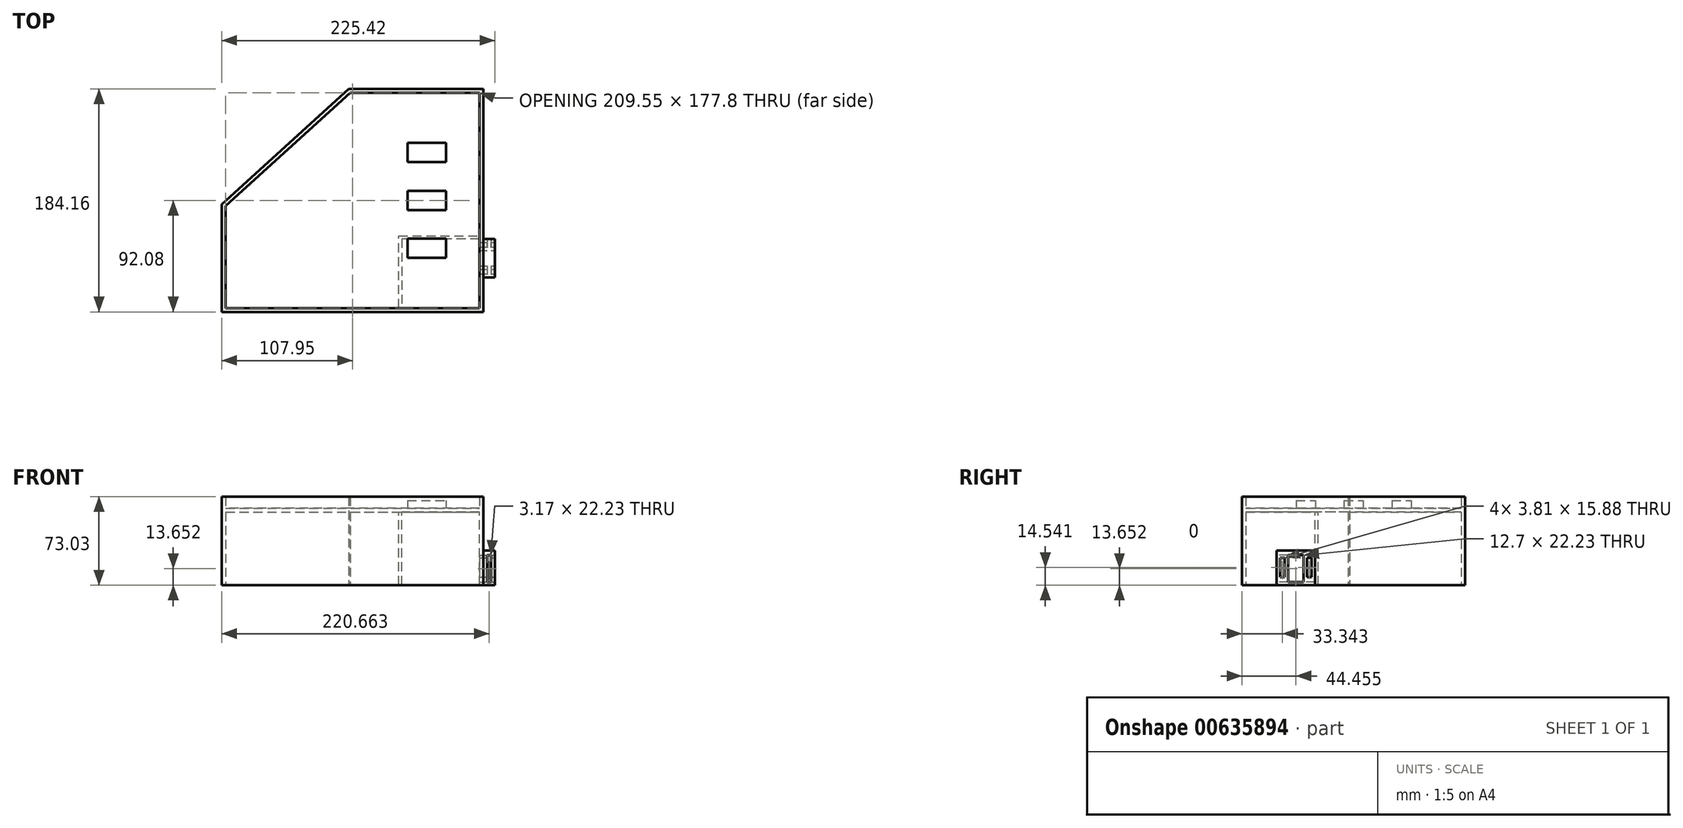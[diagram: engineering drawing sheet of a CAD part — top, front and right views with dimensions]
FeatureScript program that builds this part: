
annotation { "Feature Type Name" : "Feature", "Feature Type Description" : "" }
export const myFeature = defineFeature(function(context is Context, id is Id, definition is map)
    precondition{}
    {
        {
            var Q0;
            Q0=qCreatedBy(makeId("Top.planeOp"),FACE);
            var sketch = newSketch(context, id + "F0", { "sketchPlane" : qUnion([Q0])});
            skLineSegment(sketch, "E0.bottom", {"start": v(-3.18, 92.08) * mm, "end": v(107.95, 92.08) * mm});
            skLineSegment(sketch, "E0.top", {"start": v(-107.95, -92.08) * mm, "end": v(107.95, -92.08) * mm});
            skLineSegment(sketch, "E0.left", {"start": v(-107.95, -3.18) * mm, "end": v(-107.95, -92.07) * mm});
            skLineSegment(sketch, "E0.right", {"start": v(107.95, 92.07) * mm, "end": v(107.95, -92.08) * mm});
            skPoint(sketch, "E0.middle", {"position": v(0, 0) * mm});
            skLineSegment(sketch, "E1", {"start": v(-107.95, -3.18) * mm, "end": v(-3.18, 92.08) * mm});
            skPoint(sketch, "E2.orphan", {"position": v(-107.95, 92.08) * mm});
            skSolve(sketch);
        }
        {
            var Q0;
            Q0 = qSketchRegion(id + "F0", true);
            extrude(context, id + "F1", {"entities" : qUnion([Q0]), "depth" : 63.5 * mm, "offsetDistance" : 25.4 * mm});
        }
        {
            var Q0;
            Q0=makeQuery(id+"F1.opExtrude","CAP_FACE",FACE,{"disambiguationData":[OSD([sQuery(id+"F0.wireOp",EDGE,"E0.bottom"),sQuery(id+"F0.wireOp",EDGE,"E0.top"),sQuery(id+"F0.wireOp",EDGE,"E0.left"),sQuery(id+"F0.wireOp",EDGE,"E0.right"),sQuery(id+"F0.wireOp",EDGE,"E1")])],"isStart":true});
            shell(context, id + "F2", {"entities" : qUnion([Q0]), "thickness" : 3.17 * mm});
        }
        {
            var Q0;
            Q0=makeQuery(id+"F1.opExtrude","CAP_FACE",FACE,{"disambiguationData":[OSD([sQuery(id+"F0.wireOp",EDGE,"E0.bottom"),sQuery(id+"F0.wireOp",EDGE,"E0.top"),sQuery(id+"F0.wireOp",EDGE,"E0.left"),sQuery(id+"F0.wireOp",EDGE,"E0.right"),sQuery(id+"F0.wireOp",EDGE,"E1")])],"isStart":false});
            var sketch = newSketch(context, id + "F3", { "sketchPlane" : qUnion([Q0])});
            skLineSegment(sketch, "E3.0.0", {"start": v(-3.18, 92.08) * mm, "end": v(-107.95, -3.18) * mm});
            skLineSegment(sketch, "E3.0.1", {"start": v(-107.95, -3.18) * mm, "end": v(-107.95, -92.07) * mm});
            skLineSegment(sketch, "E3.0.2", {"start": v(-107.95, -92.08) * mm, "end": v(107.95, -92.08) * mm});
            skLineSegment(sketch, "E3.0.3", {"start": v(107.95, -92.08) * mm, "end": v(107.95, 92.07) * mm});
            skLineSegment(sketch, "E3.0.4", {"start": v(107.95, 92.08) * mm, "end": v(-3.18, 92.08) * mm});
            skLineSegment(sketch, "E4.0", {"start": v(-104.78, -88.9) * mm, "end": v(104.77, -88.9) * mm});
            skLineSegment(sketch, "E4.1", {"start": v(-104.78, -4.58) * mm, "end": v(-104.78, -88.9) * mm});
            skLineSegment(sketch, "E4.2", {"start": v(104.77, -88.9) * mm, "end": v(104.78, 88.9) * mm});
            skLineSegment(sketch, "E4.3", {"start": v(104.78, 88.9) * mm, "end": v(-1.95, 88.9) * mm});
            skLineSegment(sketch, "E4.4", {"start": v(-1.95, 88.9) * mm, "end": v(-104.78, -4.58) * mm});
            skSolve(sketch);
        }
        {
            var Q0;
            Q0 = qSketchRegion(id + "F3", true);
            extrude(context, id + "F4", {"entities" : qUnion([Q0]), "operationType" : NewBodyOperationType.ADD, "depth" : 9.52 * mm, "offsetDistance" : 25.4 * mm});
        }
        {
            var Q0;
            Q0=makeQuery(id+"F1.opExtrude","CAP_FACE",FACE,{"disambiguationData":[OSD([sQuery(id+"F0.wireOp",EDGE,"E0.bottom"),sQuery(id+"F0.wireOp",EDGE,"E0.top"),sQuery(id+"F0.wireOp",EDGE,"E0.left"),sQuery(id+"F0.wireOp",EDGE,"E0.right"),sQuery(id+"F0.wireOp",EDGE,"E1")])],"isStart":false});
            var sketch = newSketch(context, id + "F5", { "sketchPlane" : qUnion([Q0])});
            skLineSegment(sketch, "E5.bottom", {"start": v(45.27, 31.59) * mm, "end": v(77.02, 31.59) * mm});
            skLineSegment(sketch, "E5.top", {"start": v(45.27, 47.46) * mm, "end": v(77.02, 47.46) * mm});
            skLineSegment(sketch, "E5.left", {"start": v(45.27, 31.59) * mm, "end": v(45.27, 47.46) * mm});
            skLineSegment(sketch, "E5.right", {"start": v(77.02, 31.59) * mm, "end": v(77.02, 47.46) * mm});
            skPoint(sketch, "E5.middle", {"position": v(61.15, 39.52) * mm});
            skLineSegment(sketch, "E6.bottom", {"start": v(45.27, -7.94) * mm, "end": v(77.02, -7.94) * mm});
            skLineSegment(sketch, "E6.top", {"start": v(45.27, 7.94) * mm, "end": v(77.02, 7.94) * mm});
            skLineSegment(sketch, "E6.left", {"start": v(45.27, -7.94) * mm, "end": v(45.27, 7.94) * mm});
            skLineSegment(sketch, "E6.right", {"start": v(77.02, -7.94) * mm, "end": v(77.02, 7.94) * mm});
            skPoint(sketch, "E6.middle", {"position": v(61.15, 0) * mm});
            skLineSegment(sketch, "E7.bottom", {"start": v(45.27, -47.46) * mm, "end": v(77.02, -47.46) * mm});
            skLineSegment(sketch, "E7.top", {"start": v(45.27, -31.59) * mm, "end": v(77.02, -31.59) * mm});
            skLineSegment(sketch, "E7.left", {"start": v(45.27, -47.46) * mm, "end": v(45.27, -31.59) * mm});
            skLineSegment(sketch, "E7.right", {"start": v(77.02, -47.46) * mm, "end": v(77.02, -31.59) * mm});
            skPoint(sketch, "E7.middle", {"position": v(61.15, -39.52) * mm});
            skLineSegment(sketch, "E8", {"start": v(77.02, 31.59) * mm, "end": v(77.02, 7.94) * mm, "construction": true});
            skLineSegment(sketch, "E9", {"start": v(77.02, -7.94) * mm, "end": v(77.02, -31.59) * mm, "construction": true});
            skLineSegment(sketch, "E10", {"start": v(77.02, -47.46) * mm, "end": v(77.02, -88.9) * mm});
            skLineSegment(sketch, "E11", {"start": v(77.02, 47.46) * mm, "end": v(77.02, 88.9) * mm, "construction": true});
            skSolve(sketch);
        }
        {
            var Q0;
            Q0 = qSketchRegion(id + "F5", true);
            extrude(context, id + "F6", {"entities" : qUnion([Q0]), "operationType" : NewBodyOperationType.ADD, "depth" : 6.35 * mm, "offsetDistance" : 25.4 * mm});
        }
        {
            var Q0;
            Q0=makeQuery(id+"F2.opShell","OFFSET_FACE",FACE,{"disambiguationData":[OSD([sQuery(id+"F0.wireOp",EDGE,"E0.bottom"),sQuery(id+"F0.wireOp",EDGE,"E0.top"),sQuery(id+"F0.wireOp",EDGE,"E0.left"),sQuery(id+"F0.wireOp",EDGE,"E0.right"),sQuery(id+"F0.wireOp",EDGE,"E1")])]});
            var sketch = newSketch(context, id + "F7", { "sketchPlane" : qUnion([Q0])});
            skLineSegment(sketch, "E12", {"start": v(104.78, 31.75) * mm, "end": v(40.54, 31.75) * mm});
            skLineSegment(sketch, "E13", {"start": v(40.54, 31.75) * mm, "end": v(40.54, 88.9) * mm});
            skLineSegment(sketch, "E14", {"start": v(40.54, 88.9) * mm, "end": v(38, 88.9) * mm});
            skLineSegment(sketch, "E15", {"start": v(38, 88.9) * mm, "end": v(38, 29.2) * mm});
            skLineSegment(sketch, "E16", {"start": v(38, 29.2) * mm, "end": v(104.78, 29.2) * mm});
            skLineSegment(sketch, "E17", {"start": v(104.77, 29.2) * mm, "end": v(104.77, 31.75) * mm});
            skSolve(sketch);
        }
        {
            var Q0;
            Q0 = qSketchRegion(id + "F7", true);
            var Q1;
            Q1=makeQuery(id+"F1.opExtrude","CAP_FACE",FACE,{"disambiguationData":[OSD([sQuery(id+"F0.wireOp",EDGE,"E0.bottom"),sQuery(id+"F0.wireOp",EDGE,"E0.top"),sQuery(id+"F0.wireOp",EDGE,"E0.left"),sQuery(id+"F0.wireOp",EDGE,"E0.right"),sQuery(id+"F0.wireOp",EDGE,"E1")])],"isStart":true});
            extrude(context, id + "F8", {"entities" : qUnion([Q0]), "operationType" : NewBodyOperationType.ADD, "endBound" : BoundingType.UP_TO_SURFACE, "depth" : 25.4 * mm, "endBoundEntityFace" : qUnion([Q1]), "offsetDistance" : 25.4 * mm});
        }
        {
            var Q0;
            Q0=makeQuery(id+"F4.boolean.opBoolean","MERGE",FACE,{"derivedFrom":[makeQuery(id+"F1.opExtrude","SWEPT_FACE",FACE,{"disambiguationData":[OSD([sQuery(id+"F0.wireOp",EDGE,"E0.right")])]}),makeQuery(id+"F4.opExtrude","SWEPT_FACE",FACE,{"disambiguationData":[OSD([sQuery(id+"F3.wireOp",EDGE,"E3.0.3")])]})]});
            var sketch = newSketch(context, id + "F9", { "sketchPlane" : qUnion([Q0])});
            skLineSegment(sketch, "E18.bottom", {"start": v(-63.5, 0) * mm, "end": v(-31.75, 0) * mm});
            skLineSegment(sketch, "E18.top", {"start": v(-63.5, 28.58) * mm, "end": v(-31.75, 28.58) * mm});
            skLineSegment(sketch, "E18.left", {"start": v(-63.5, 0) * mm, "end": v(-63.5, 28.58) * mm});
            skLineSegment(sketch, "E18.right", {"start": v(-31.75, 0) * mm, "end": v(-31.75, 28.58) * mm});
            skSolve(sketch);
        }
        {
            var Q0;
            Q0 = qSketchRegion(id + "F9", true);
            extrude(context, id + "F10", {"entities" : qUnion([Q0]), "operationType" : NewBodyOperationType.ADD, "depth" : 9.52 * mm, "offsetDistance" : 25.4 * mm});
        }
        {
            var Q0;
            Q0=makeQuery(id+"F10.opExtrude","CAP_FACE",FACE,{"disambiguationData":[OSD([sQuery(id+"F9.wireOp",EDGE,"E18.bottom"),sQuery(id+"F9.wireOp",EDGE,"E18.top"),sQuery(id+"F9.wireOp",EDGE,"E18.left"),sQuery(id+"F9.wireOp",EDGE,"E18.right")])],"isStart":false});
            var sketch = newSketch(context, id + "F11", { "sketchPlane" : qUnion([Q0])});
            skLineSegment(sketch, "E19.bottom", {"start": v(-41.27, 24.77) * mm, "end": v(-53.97, 24.77) * mm});
            skLineSegment(sketch, "E19.top", {"start": v(-41.27, 2.54) * mm, "end": v(-53.97, 2.54) * mm});
            skLineSegment(sketch, "E19.left", {"start": v(-41.27, 24.77) * mm, "end": v(-41.27, 2.54) * mm});
            skLineSegment(sketch, "E19.right", {"start": v(-53.97, 24.77) * mm, "end": v(-53.97, 2.54) * mm});
            skLineSegment(sketch, "E20", {"start": v(-53.97, 24.77) * mm, "end": v(-63.5, 24.77) * mm, "construction": true});
            skLineSegment(sketch, "E21", {"start": v(-41.27, 24.77) * mm, "end": v(-31.75, 24.77) * mm, "construction": true});
            skLineSegment(sketch, "E22.bottom", {"start": v(-56.83, 22.48) * mm, "end": v(-60.64, 22.48) * mm});
            skLineSegment(sketch, "E22.top", {"start": v(-56.83, 6.6) * mm, "end": v(-60.64, 6.6) * mm});
            skLineSegment(sketch, "E22.left", {"start": v(-56.83, 22.48) * mm, "end": v(-56.83, 6.6) * mm});
            skLineSegment(sketch, "E22.right", {"start": v(-60.64, 22.48) * mm, "end": v(-60.64, 6.6) * mm});
            skLineSegment(sketch, "E23", {"start": v(-56.83, 6.6) * mm, "end": v(-53.97, 6.6) * mm, "construction": true});
            skLineSegment(sketch, "E24", {"start": v(-60.64, 6.6) * mm, "end": v(-63.5, 6.6) * mm, "construction": true});
            skLineSegment(sketch, "E25", {"start": v(-47.62, 24.77) * mm, "end": v(-47.62, 2.54) * mm, "construction": true});
            skLineSegment(sketch, "E26.MirrorCS", {"start": v(-38.42, 6.6) * mm, "end": v(-34.6, 6.6) * mm});
            skLineSegment(sketch, "E27.MirrorCS", {"start": v(-38.42, 22.48) * mm, "end": v(-34.6, 22.48) * mm});
            skLineSegment(sketch, "E28.MirrorCS", {"start": v(-34.6, 6.6) * mm, "end": v(-31.75, 6.6) * mm, "construction": true});
            skLineSegment(sketch, "E29.MirrorCS", {"start": v(-38.42, 22.48) * mm, "end": v(-38.42, 6.6) * mm});
            skLineSegment(sketch, "E30.MirrorCS", {"start": v(-34.6, 22.48) * mm, "end": v(-34.6, 6.6) * mm});
            skSolve(sketch);
        }
        {
            var Q0;
            Q0 = qSketchRegion(id + "F11", true);
            extrude(context, id + "F12", {"entities" : qUnion([Q0]), "operationType" : NewBodyOperationType.REMOVE, "oppositeDirection" : true, "depth" : 25.65 * mm, "offsetDistance" : 25.4 * mm});
        }
        {
            var Q0;
            Q0=makeQuery(id+"F10.opExtrude","SWEPT_FACE",FACE,{"disambiguationData":[OSD([sQuery(id+"F9.wireOp",EDGE,"E18.left")])]});
            var sketch = newSketch(context, id + "F13", { "sketchPlane" : qUnion([Q0])});
            skLineSegment(sketch, "E31.bottom", {"start": v(111.13, 24.77) * mm, "end": v(114.3, 24.77) * mm});
            skLineSegment(sketch, "E31.top", {"start": v(111.13, 2.54) * mm, "end": v(114.3, 2.54) * mm});
            skLineSegment(sketch, "E31.left", {"start": v(111.13, 24.77) * mm, "end": v(111.13, 2.54) * mm});
            skLineSegment(sketch, "E31.right", {"start": v(114.3, 24.77) * mm, "end": v(114.3, 2.54) * mm});
            skLineSegment(sketch, "E32", {"start": v(111.13, 24.77) * mm, "end": v(107.95, 24.77) * mm, "construction": true});
            skLineSegment(sketch, "E33", {"start": v(114.3, 24.77) * mm, "end": v(117.48, 24.77) * mm, "construction": true});
            skSolve(sketch);
        }
        {
            var Q0;
            Q0 = qSketchRegion(id + "F13", true);
            extrude(context, id + "F14", {"entities" : qUnion([Q0]), "operationType" : NewBodyOperationType.REMOVE, "oppositeDirection" : true, "depth" : 127 * mm, "offsetDistance" : 25.4 * mm});
        }
    });
